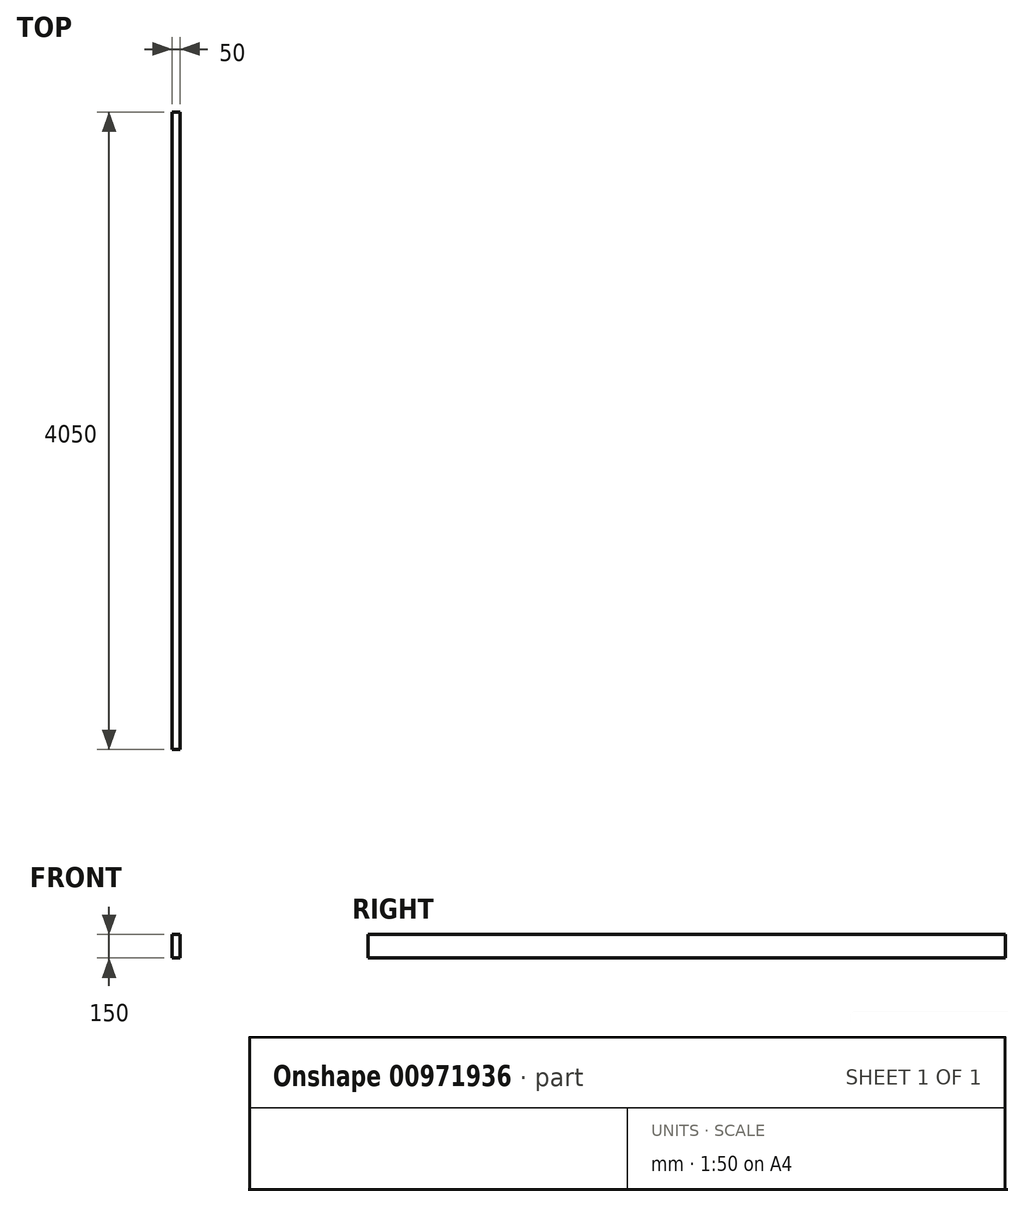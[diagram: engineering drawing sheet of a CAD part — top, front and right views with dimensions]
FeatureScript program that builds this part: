
annotation { "Feature Type Name" : "Feature", "Feature Type Description" : "" }
export const myFeature = defineFeature(function(context is Context, id is Id, definition is map)
    precondition{}
    {
        {
            var Q0;
            Q0=qCreatedBy(makeId("Front.planeOp"),FACE);
            var sketch = newSketch(context, id + "F0", { "sketchPlane" : qUnion([Q0])});
            skLineSegment(sketch, "E0.bottom", {"start": v(25, -75) * mm, "end": v(-25, -75) * mm});
            skLineSegment(sketch, "E0.top", {"start": v(25, 75) * mm, "end": v(-25, 75) * mm});
            skLineSegment(sketch, "E0.left", {"start": v(25, -75) * mm, "end": v(25, 75) * mm});
            skLineSegment(sketch, "E0.right", {"start": v(-25, -75) * mm, "end": v(-25, 75) * mm});
            skPoint(sketch, "E0.middle", {"position": v(0, 0) * mm});
            skSolve(sketch);
        }
        {
            var Q0;
            Q0 = qSketchRegion(id + "F0", true);
            extrude(context, id + "F1", {"entities" : qUnion([Q0]), "depth" : 4050 * mm, "offsetDistance" : 25 * mm});
        }
    });
